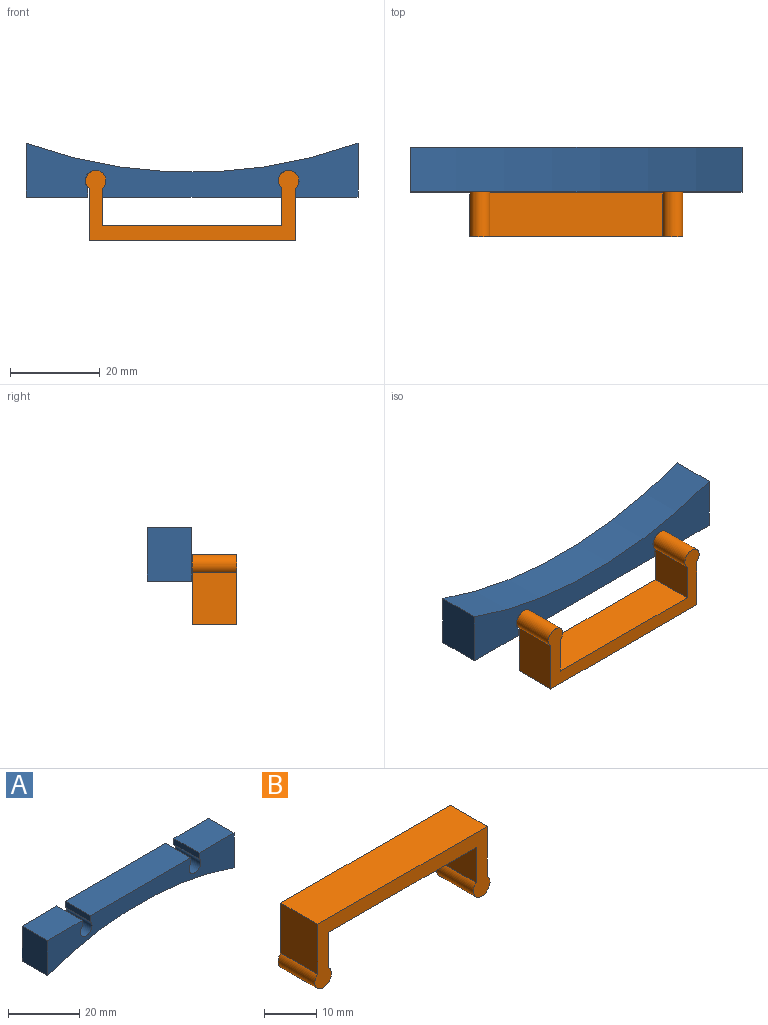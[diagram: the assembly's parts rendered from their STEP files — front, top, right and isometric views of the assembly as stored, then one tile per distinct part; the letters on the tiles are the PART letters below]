
ASSEMBLY  parts=2 mates=1
PART A: 14 faces, bbox 74x10x12 mm
  f0: plane 13.81x10mm, normal (0,0,1), area 138.1mm2, adj f2,f3,f5,f12
  f1: plane 39.8x10mm, normal (0,0,1), area 398mm2, adj f2,f3,f10,f13
  f2: plane 74x12mm, normal (0,-1,0), area 523.2mm2, adj f0,f1,f4,f5,f6,f7,f8,f9
  f3: plane 74x12mm, normal (0,1,0), area 523.2mm2, adj f0,f1,f4,f5,f6,f7,f8,f9
  f4: plane 12x10mm, normal (-1,0,0), area 120mm2, adj f2,f3,f6,f7
  f5: plane 12x10mm, normal (1,0,0), area 120mm2, adj f0,f2,f3,f7
  f6: plane 13.84x10mm, normal (0,0,1), area 138.4mm2, adj f2,f3,f4,f8
  f7: cylinder r=109mm len=74mm, axis (0,-1,0), area 755mm2, adj f2,f3,f4,f5
  f8: plane 10x2.03mm, normal (1,0,0), area 20.3mm2, adj f2,f3,f6,f9
  f9: cylinder r=2.3mm len=10mm, axis (0,-1,0), area 108.3mm2, adj f2,f3,f8,f10
  f10: plane 10x2.08mm, normal (-1,0,0), area 20.8mm2, adj f1,f2,f3,f9
  f11: cylinder r=2.3mm len=10mm, axis (0,-1,0), area 107.8mm2, adj f2,f3,f12,f13
  f12: plane 10x2.07mm, normal (-1,0,0), area 20.7mm2, adj f0,f2,f3,f11
  f13: plane 10x2.03mm, normal (1,0,0), area 20.3mm2, adj f1,f2,f3,f11
PART B: 10 faces, bbox 47.5x10x15.7 mm
  f0: cylinder r=2.25mm len=10mm, axis (0,1,0), area 108.5mm2, adj f1,f7,f8,f9
  f1: plane 10x8.32mm, normal (1,0,0), area 83.2mm2, adj f0,f2,f8,f9
  f2: plane 40x10mm, normal (0,0,-1), area 400mm2, adj f1,f3,f8,f9
  f3: plane 10x8.33mm, normal (-1,0,0), area 83.3mm2, adj f2,f4,f8,f9
  f4: cylinder r=2.25mm len=10mm, axis (0,1,0), area 108.5mm2, adj f3,f5,f8,f9
  f5: plane 11.73x10mm, normal (1,0,0), area 117.3mm2, adj f4,f6,f8,f9
  f6: plane 46x10mm, normal (0,0,1), area 460mm2, adj f5,f7,f8,f9
  f7: plane 11.73x10mm, normal (-1,0,0), area 117.3mm2, adj f0,f6,f8,f9
  f8: plane 47.5x15.66mm, normal (0,-1,0), area 236mm2, adj f0,f1,f2,f3,f4,f5,f6,f7
  f9: plane 47.5x15.66mm, normal (0,1,0), area 236mm2, adj f0,f1,f2,f3,f4,f5,f6,f7
PLACE A rot(axis=(0,1,0),180deg) t=(45.2,-4.95,13.85)mm
PLACE B rot(axis=(0,1,0),180deg) t=(45.26,-13.17,20.86)mm
MATE slider A.f9 <-> B.f0  axis (0,-1,0) through (68.71,-13.17,5.53)mm
